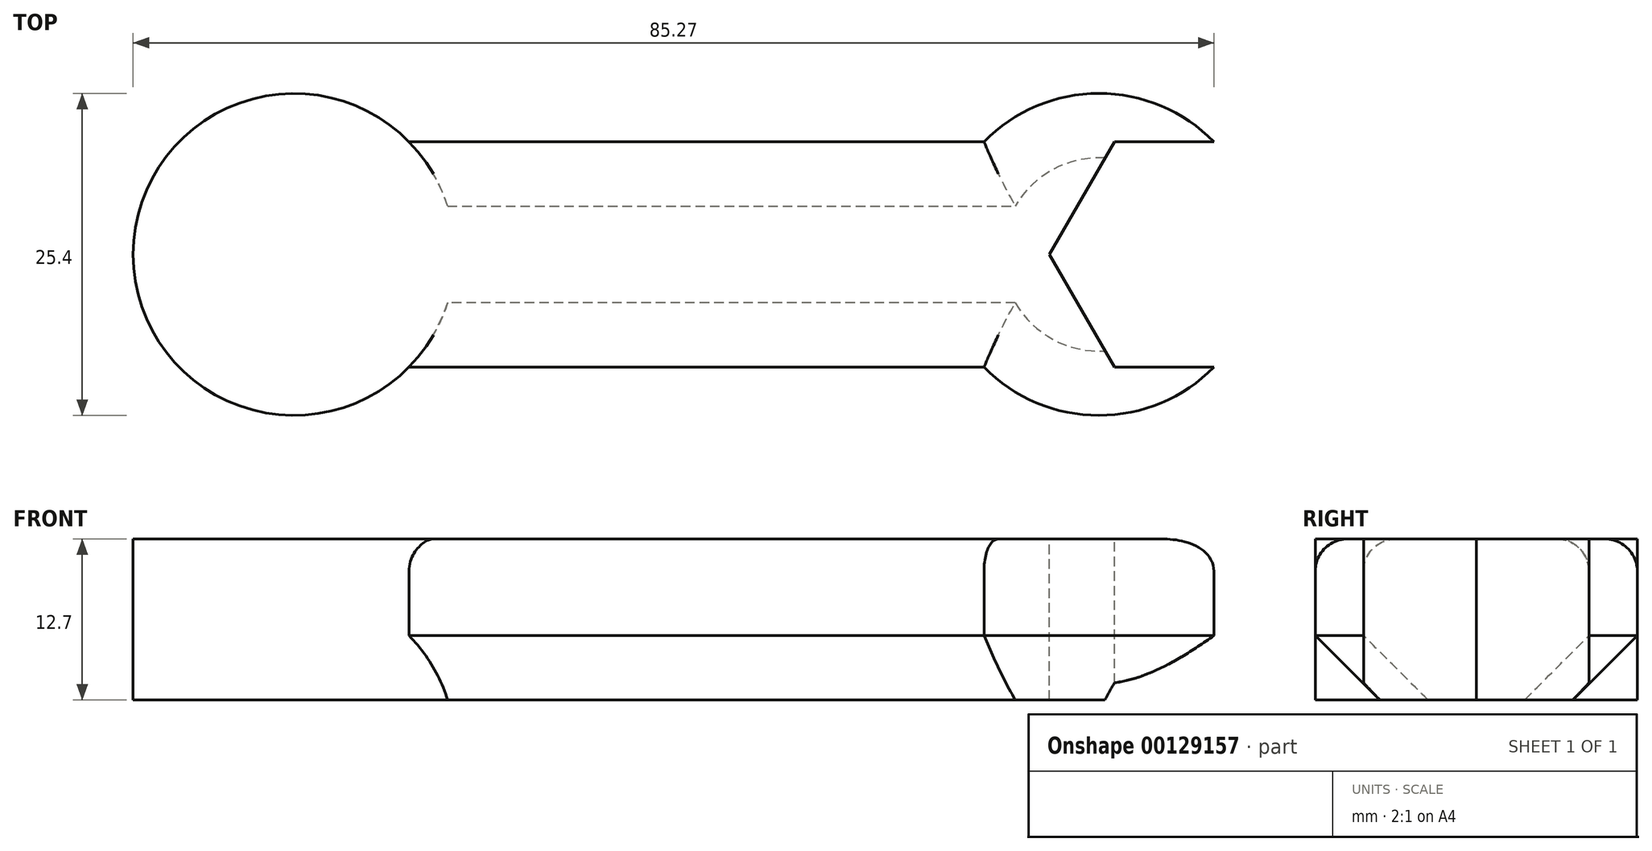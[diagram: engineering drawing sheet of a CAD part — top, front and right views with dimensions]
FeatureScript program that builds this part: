
annotation { "Feature Type Name" : "Feature", "Feature Type Description" : "" }
export const myFeature = defineFeature(function(context is Context, id is Id, definition is map)
    precondition{}
    {
        {
            var Q0;
            Q0=qCreatedBy(makeId("Top.planeOp"),FACE);
            var sketch = newSketch(context, id + "F0", { "sketchPlane" : qUnion([Q0])});
            skArc(sketch, "E0", {"start": v(-22.68, 8.89) * mm, "mid": v(-44.45, 0) * mm, "end": v(-22.68, -8.9) * mm});
            skArc(sketch, "E1", {"start": v(22.68, -8.9) * mm, "mid": v(44.45, 0) * mm, "end": v(22.68, 8.89) * mm});
            skLineSegment(sketch, "E2", {"start": v(-22.68, 8.89) * mm, "end": v(22.68, 8.89) * mm});
            skLineSegment(sketch, "E3", {"start": v(-22.68, -8.9) * mm, "end": v(22.68, -8.9) * mm});
            skLineSegment(sketch, "E4", {"start": v(-31.75, 0) * mm, "end": v(31.75, 0) * mm});
            skSolve(sketch);
        }
        {
            var Q0;
            Q0 = qSketchRegion(id + "F0", true);
            extrude(context, id + "F1", {"entities" : qUnion([Q0]), "endBound" : BoundingType.SYMMETRIC, "oppositeDirection" : true, "depth" : 12.7 * mm});
        }
        {
            var Q0;
            Q0=makeQuery(id+"F1.opExtrude","CAP_FACE",FACE,{"disambiguationData":[OSD([sQuery(id+"F0.wireOp",EDGE,"E0"),sQuery(id+"F0.wireOp",EDGE,"E1"),sQuery(id+"F0.wireOp",EDGE,"E2"),sQuery(id+"F0.wireOp",EDGE,"E3")])],"isStart":true});
            var sketch = newSketch(context, id + "F2", { "sketchPlane" : qUnion([Q0])});
            skCircle(sketch, "E5.cCircle", {"center": v(38.1, 0) * mm, "radius": 8.9 * mm, "construction": true});
            skLineSegment(sketch, "E5.0", {"start": v(32.97, -8.89) * mm, "end": v(27.83, 0) * mm});
            skLineSegment(sketch, "E5.1", {"start": v(27.83, 0) * mm, "end": v(32.97, 8.9) * mm});
            skLineSegment(sketch, "E5.2", {"start": v(32.97, 8.9) * mm, "end": v(43.23, 8.9) * mm});
            skLineSegment(sketch, "E5.3", {"start": v(43.23, 8.9) * mm, "end": v(48.37, 0) * mm});
            skLineSegment(sketch, "E5.4", {"start": v(48.37, 0) * mm, "end": v(43.23, -8.9) * mm});
            skLineSegment(sketch, "E5.5", {"start": v(43.23, -8.89) * mm, "end": v(32.97, -8.89) * mm});
            skPoint(sketch, "E5.0.midPoint", {"position": v(30.4, -4.44) * mm});
            skSolve(sketch);
        }
        {
            var Q0;
            Q0 = qSketchRegion(id + "F2", true);
            extrude(context, id + "F3", {"entities" : qUnion([Q0]), "operationType" : NewBodyOperationType.REMOVE, "endBound" : BoundingType.THROUGH_ALL, "oppositeDirection" : true, "depth" : 25.4 * mm});
        }
        {
            var Q0;
            Q0=makeQuery(id+"F1.opExtrude","CAP_EDGE",EDGE,{"disambiguationData":[OSD([sQuery(id+"F0.wireOp",EDGE,"E3")])],"isStart":true});
            var Q1;
            {var subQ0=sQuery(id+"F0.wireOp",EDGE,"E3");var subQ1=sQuery(id+"F0.wireOp",EDGE,"E1");Q1=makeQuery(id+"F3.boolean.opBoolean","SPLIT",EDGE,{"disambiguationData":[TD([makeQuery(id+"F1.opExtrude","SWEPT_FACE",FACE,{"disambiguationData":[OSD([subQ0])]})])],"derivedFrom":makeQuery(id+"F1.opExtrude","CAP_EDGE",EDGE,{"disambiguationData":[OSD([subQ1])],"isStart":true})});}
            var Q2;
            Q2=makeQuery(id+"F1.opExtrude","CAP_EDGE",EDGE,{"disambiguationData":[OSD([sQuery(id+"F0.wireOp",EDGE,"E2")])],"isStart":true});
            var Q3;
            {var subQ0=sQuery(id+"F0.wireOp",EDGE,"E2");var subQ1=sQuery(id+"F0.wireOp",EDGE,"E1");Q3=makeQuery(id+"F3.boolean.opBoolean","SPLIT",EDGE,{"disambiguationData":[TD([makeQuery(id+"F1.opExtrude","SWEPT_FACE",FACE,{"disambiguationData":[OSD([subQ0])]})])],"derivedFrom":makeQuery(id+"F1.opExtrude","CAP_EDGE",EDGE,{"disambiguationData":[OSD([subQ1])],"isStart":true})});}
            fillet(context, id + "F4", {"entities" : qUnion([Q0, Q1, Q2, Q3]), "radius" : 2.54 * mm, "tangentPropagation" : true, "allowEdgeOverflow" : false});
        }
        {
            var Q0;
            Q0=makeQuery(id+"F1.opExtrude","CAP_EDGE",EDGE,{"disambiguationData":[OSD([sQuery(id+"F0.wireOp",EDGE,"E2")])],"isStart":false});
            var Q1;
            {var subQ0=sQuery(id+"F0.wireOp",EDGE,"E2");var subQ1=sQuery(id+"F0.wireOp",EDGE,"E1");Q1=makeQuery(id+"F3.boolean.opBoolean","SPLIT",EDGE,{"disambiguationData":[TD([makeQuery(id+"F1.opExtrude","SWEPT_FACE",FACE,{"disambiguationData":[OSD([subQ0])]})])],"derivedFrom":makeQuery(id+"F1.opExtrude","CAP_EDGE",EDGE,{"disambiguationData":[OSD([subQ1])],"isStart":false})});}
            var Q2;
            Q2=makeQuery(id+"F1.opExtrude","CAP_EDGE",EDGE,{"disambiguationData":[OSD([sQuery(id+"F0.wireOp",EDGE,"E3")])],"isStart":false});
            var Q3;
            {var subQ0=sQuery(id+"F0.wireOp",EDGE,"E3");var subQ1=sQuery(id+"F0.wireOp",EDGE,"E1");Q3=makeQuery(id+"F3.boolean.opBoolean","SPLIT",EDGE,{"disambiguationData":[TD([makeQuery(id+"F1.opExtrude","SWEPT_FACE",FACE,{"disambiguationData":[OSD([subQ0])]})])],"derivedFrom":makeQuery(id+"F1.opExtrude","CAP_EDGE",EDGE,{"disambiguationData":[OSD([subQ1])],"isStart":false})});}
            chamfer(context, id + "F5", {"entities" : qUnion([Q0, Q1, Q2, Q3]), "width" : 5.08 * mm, "tangentPropagation" : true});
        }
    });
